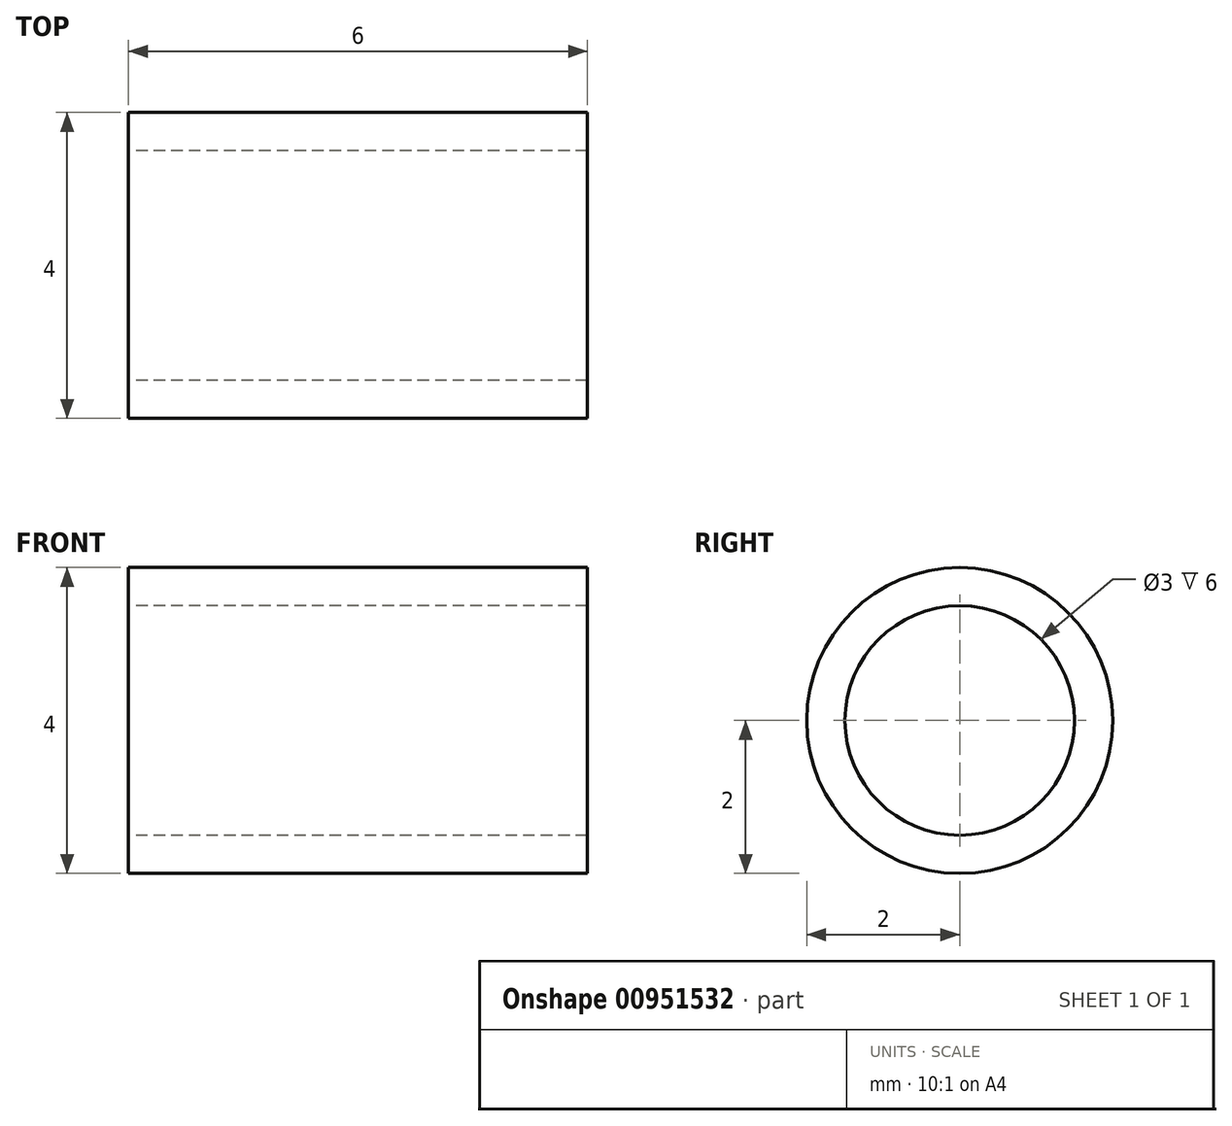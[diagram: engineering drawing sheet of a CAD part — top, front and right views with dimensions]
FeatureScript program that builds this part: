
annotation { "Feature Type Name" : "Feature", "Feature Type Description" : "" }
export const myFeature = defineFeature(function(context is Context, id is Id, definition is map)
    precondition{}
    {
        {
            var Q0;
            Q0=qCreatedBy(makeId("Right.planeOp"),FACE);
            var sketch = newSketch(context, id + "F0", { "sketchPlane" : qUnion([Q0])});
            skCircle(sketch, "E0", {"center": v(0, 0) * mm, "radius": 1.5 * mm});
            skCircle(sketch, "E1", {"center": v(0, 0) * mm, "radius": 2 * mm});
            skSolve(sketch);
        }
        {
            var Q0;
            Q0 = qSketchRegion(id + "F0", true);
            extrude(context, id + "F1", {"entities" : qUnion([Q0]), "depth" : 6 * mm, "offsetDistance" : 25 * mm});
        }
    });
